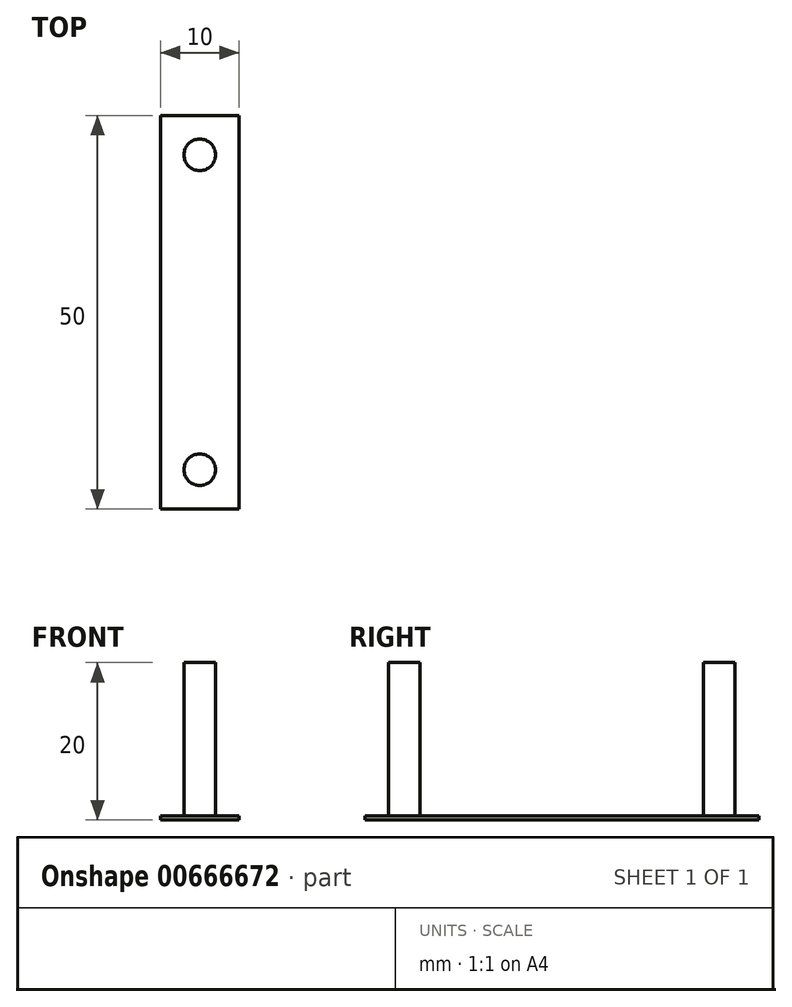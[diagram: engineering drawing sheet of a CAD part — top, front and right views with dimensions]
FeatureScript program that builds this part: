
annotation { "Feature Type Name" : "Feature", "Feature Type Description" : "" }
export const myFeature = defineFeature(function(context is Context, id is Id, definition is map)
    precondition{}
    {
        {
            var Q0;
            Q0=qCreatedBy(makeId("Top.planeOp"),FACE);
            var sketch = newSketch(context, id + "F0", { "sketchPlane" : qUnion([Q0])});
            skLineSegment(sketch, "E0.bottom", {"start": v(0, 0) * mm, "end": v(-10, 0) * mm});
            skLineSegment(sketch, "E0.top", {"start": v(0, 50) * mm, "end": v(-10, 50) * mm});
            skLineSegment(sketch, "E0.left", {"start": v(0, 0) * mm, "end": v(0, 50) * mm});
            skLineSegment(sketch, "E0.right", {"start": v(-10, 0) * mm, "end": v(-10, 50) * mm});
            skLineSegment(sketch, "E1", {"start": v(-5, 50) * mm, "end": v(-5, 0) * mm, "construction": true});
            skCircle(sketch, "E2", {"center": v(-5, 45) * mm, "radius": 2 * mm});
            skCircle(sketch, "E3", {"center": v(-5, 5) * mm, "radius": 2 * mm});
            skSolve(sketch);
        }
        {
            var Q0;
            Q0=makeQuery(id+"F0.imprint","IMPRINT",FACE,{"disambiguationData":[TD([[makeQuery(id+"F0.imprint","IMPRINT",EDGE,{"derivedFrom":sQuery(id+"F0.wireOp",EDGE,"E0.bottom")}),-1.0]])]});
            extrude(context, id + "F1", {"entities" : qUnion([Q0]), "depth" : .5 * mm, "offsetDistance" : 25 * mm});
        }
        {
            var Q0;
            Q0=makeQuery(id+"F0.imprint","IMPRINT",FACE,{"disambiguationData":[TD([[makeQuery(id+"F0.imprint","IMPRINT",EDGE,{"derivedFrom":sQuery(id+"F0.wireOp",EDGE,"E3")}),1.0]])]});
            var Q1;
            Q1=makeQuery(id+"F0.imprint","IMPRINT",FACE,{"disambiguationData":[TD([[makeQuery(id+"F0.imprint","IMPRINT",EDGE,{"derivedFrom":sQuery(id+"F0.wireOp",EDGE,"E2")}),1.0]])]});
            extrude(context, id + "F2", {"entities" : qUnion([Q0, Q1]), "operationType" : NewBodyOperationType.ADD, "depth" : 20 * mm, "offsetDistance" : 25 * mm});
        }
    });
